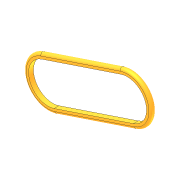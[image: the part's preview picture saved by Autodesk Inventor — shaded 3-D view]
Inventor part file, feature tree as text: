
AUTODESK INVENTOR PART (.ipt)
format: ipt  version: 2012 (Build 160160000, 160)  size: 103,424 bytes
history: native  units: in
note: dims shown in document units (in); Inventor stores cm internally (conversion verified against a paired STEP export)
features: extrude x1, fillet x1, sketch x1
ambient origin geometry x8: Origin, YZ Plane, XZ Plane, XY Plane, X Axis, Y Axis, Z Axis, Center Point
bodies: Solid1 (feature_tree)
feature tree (3):
  extrude  "Extrusion1"  Depth=3.25in
  fillet  "Fillet1"  Radius=0.1875in
  sketch  "Sketch1"  dims[d0=0.75in d1=3.25in d2=0.1875in d3=0.1875in d4=0.0in d5=0.0938in]
